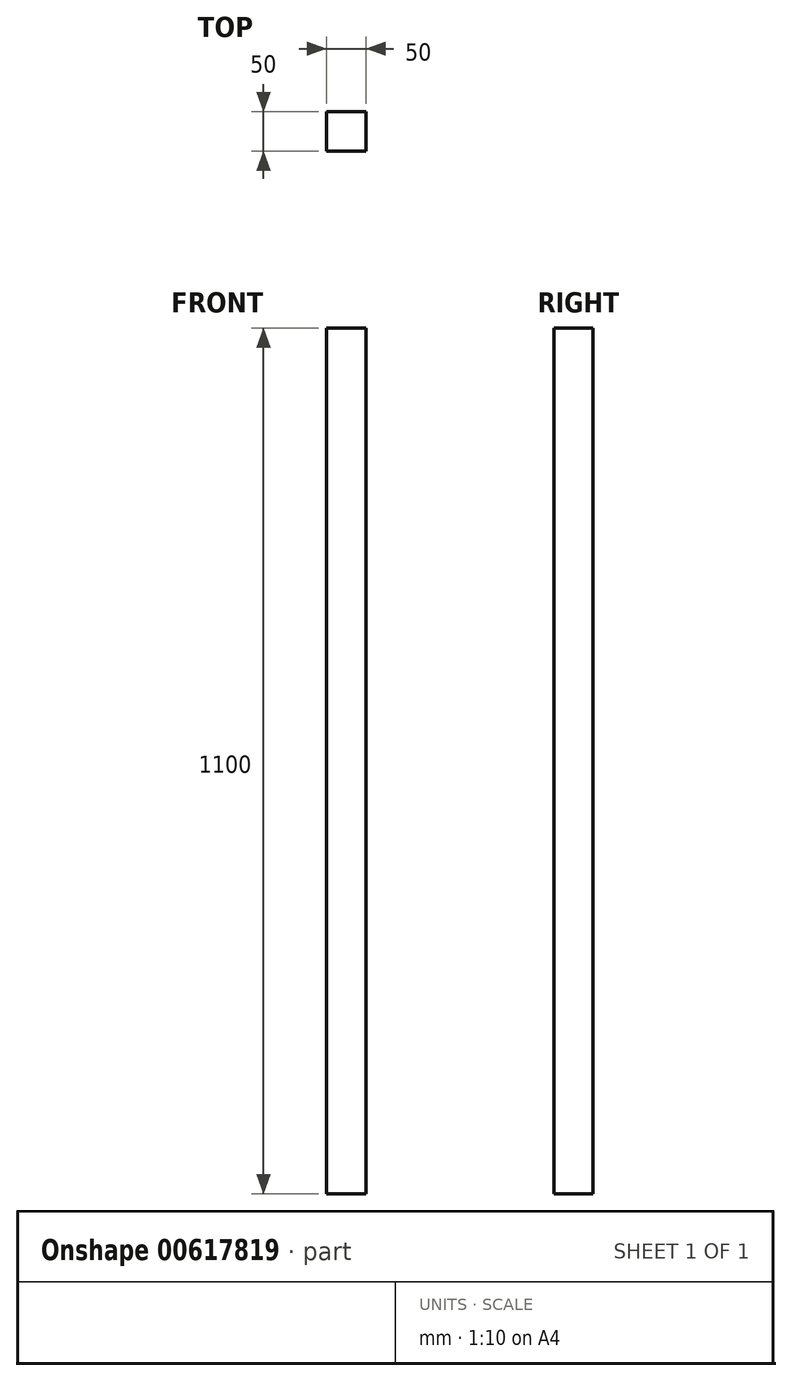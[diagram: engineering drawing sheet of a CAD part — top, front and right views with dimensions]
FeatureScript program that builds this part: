
annotation { "Feature Type Name" : "Feature", "Feature Type Description" : "" }
export const myFeature = defineFeature(function(context is Context, id is Id, definition is map)
    precondition{}
    {
        {
            var Q0;
            Q0=qCreatedBy(makeId("Front.planeOp"),FACE);
            var sketch = newSketch(context, id + "F0", { "sketchPlane" : qUnion([Q0])});
            skLineSegment(sketch, "E0.bottom", {"start": v(-51.53, 1040.35) * mm, "end": v(-1.53, 1040.35) * mm});
            skLineSegment(sketch, "E0.top", {"start": v(-51.53, -59.65) * mm, "end": v(-1.53, -59.65) * mm});
            skLineSegment(sketch, "E0.left", {"start": v(-51.53, 1040.35) * mm, "end": v(-51.53, -59.65) * mm});
            skLineSegment(sketch, "E0.right", {"start": v(-1.53, 1040.35) * mm, "end": v(-1.53, -59.65) * mm});
            skLineSegment(sketch, "E1.bottom", {"start": v(-26.53, 1040.35) * mm, "end": v(-26.53, 1040.35) * mm});
            skLineSegment(sketch, "E1.top", {"start": v(-26.53, 1040.35) * mm, "end": v(-26.53, 1040.35) * mm});
            skLineSegment(sketch, "E1.left", {"start": v(-26.53, 1040.35) * mm, "end": v(-26.53, 1040.35) * mm});
            skLineSegment(sketch, "E1.right", {"start": v(-26.53, 1040.35) * mm, "end": v(-26.53, 1040.35) * mm});
            skSolve(sketch);
        }
        {
            var Q0;
            Q0 = qSketchRegion(id + "F0", true);
            extrude(context, id + "F1", {"entities" : qUnion([Q0]), "depth" : 50 * mm, "offsetDistance" : 25 * mm});
        }
    });
